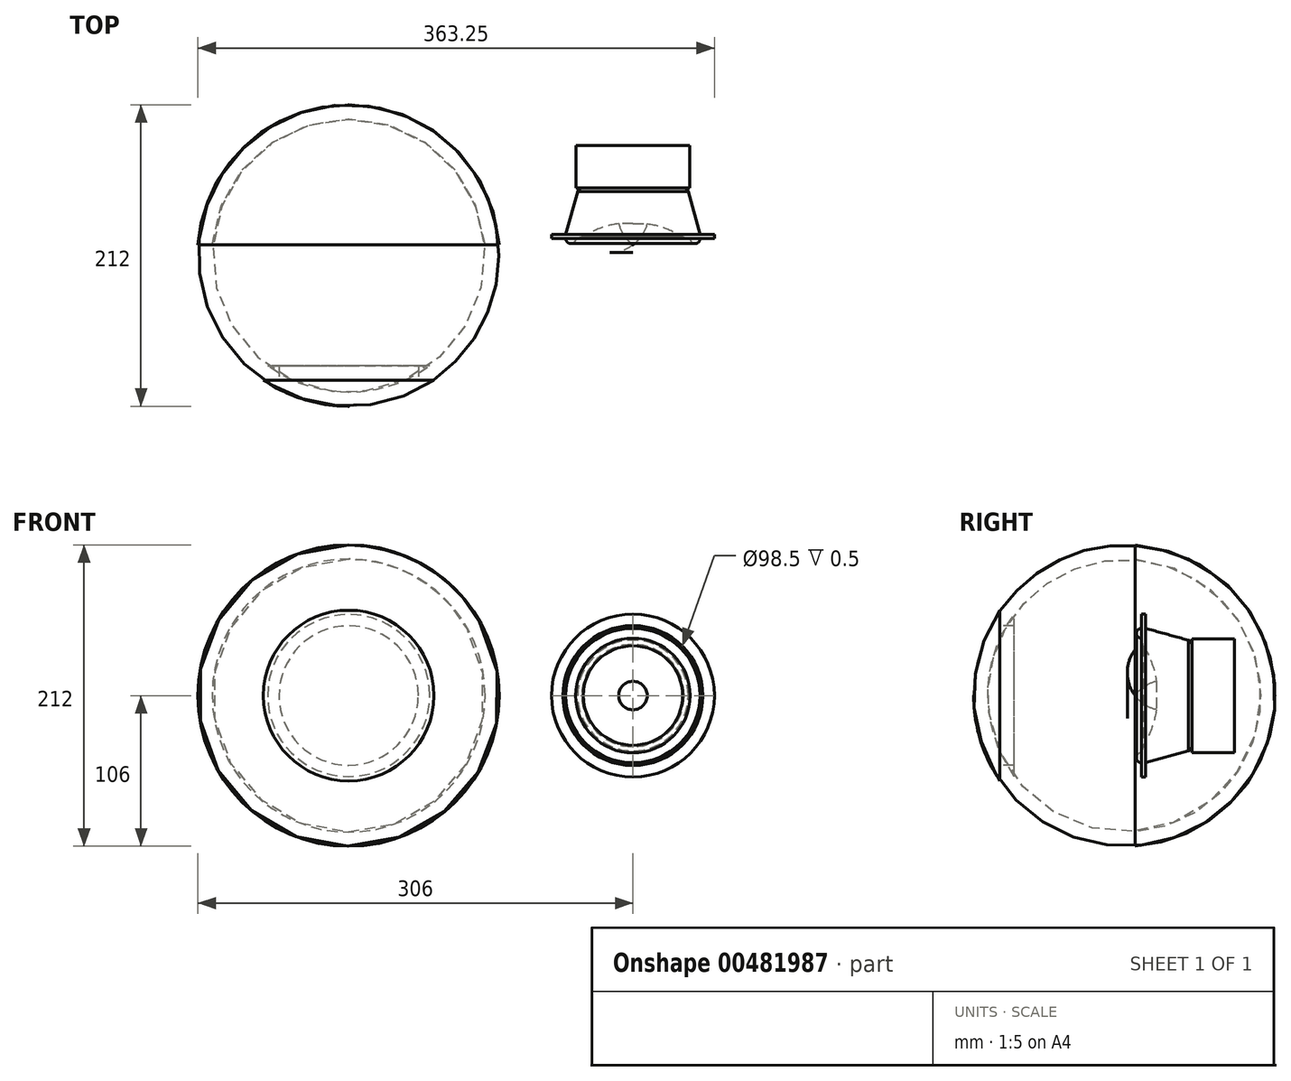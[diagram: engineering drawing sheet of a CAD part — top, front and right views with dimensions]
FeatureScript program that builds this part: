
annotation { "Feature Type Name" : "Feature", "Feature Type Description" : "" }
export const myFeature = defineFeature(function(context is Context, id is Id, definition is map)
    precondition{}
    {
        {
            var Q0;
            Q0=qCreatedBy(makeId("Top.planeOp"),FACE);
            var sketch = newSketch(context, id + "F0", { "sketchPlane" : qUnion([Q0])});
            skLineSegment(sketch, "E0", {"start": v(0, -95) * mm, "end": v(60, -95) * mm});
            skArc(sketch, "E1", {"start": v(60, -95) * mm, "mid": v(95.67, -53.63) * mm, "end": v(106, 0) * mm});
            skLineSegment(sketch, "E2", {"start": v(0, -95) * mm, "end": v(0, -85) * mm});
            skLineSegment(sketch, "E3", {"start": v(0, -85) * mm, "end": v(57, -85) * mm});
            skArc(sketch, "E4", {"start": v(57, -85) * mm, "mid": v(87.55, -47.57) * mm, "end": v(96, 0) * mm});
            skLineSegment(sketch, "E5", {"start": v(96, 0) * mm, "end": v(106, 0) * mm});
            skSolve(sketch);
        }
        {
            var Q0;
            Q0=qCreatedBy(makeId("Top.planeOp"),FACE);
            var sketch = newSketch(context, id + "F1", { "sketchPlane" : qUnion([Q0])});
            skLineSegment(sketch, "E6", {"start": v(0, -13) * mm, "end": v(0, 107) * mm, "construction": true});
            skSolve(sketch);
        }
        {
            var Q0;
            Q0 = qSketchRegion(id + "F0", true);
            var Q1;
            Q1=sQuery(id+"F1.wireOp",EDGE,"E6");
            var Q2;
            Q2=sQuery(id+"F1.wireOp",EDGE,"E6");
            revolve(context, id + "F2", {"entities" : qUnion([Q0]), "surfaceEntities" : qUnion([Q1]), "axis" : qUnion([Q2]), "revolveType" : RevolveType.FULL});
        }
        {
            var Q0;
            Q0=qCreatedBy(makeId("Top.planeOp"),FACE);
            var sketch = newSketch(context, id + "F3", { "sketchPlane" : qUnion([Q0])});
            skLineSegment(sketch, "E7", {"start": v(200, 70) * mm, "end": v(240, 70) * mm});
            skLineSegment(sketch, "E8", {"start": v(240, 70) * mm, "end": v(240, 40) * mm});
            skLineSegment(sketch, "E9", {"start": v(240, 40) * mm, "end": v(236, 40) * mm});
            skArc(sketch, "E10", {"start": v(200, 0) * mm, "mid": v(206.29, 6.64) * mm, "end": v(210, 15) * mm});
            skArc(sketch, "E11", {"start": v(235, 5.72) * mm, "mid": v(223.02, 11.76) * mm, "end": v(210, 15) * mm});
            skArc(sketch, "E12", {"start": v(240.25, 4.5) * mm, "mid": v(243.75, 1) * mm, "end": v(247.25, 4.5) * mm});
            skLineSegment(sketch, "E13", {"start": v(235, 5.72) * mm, "end": v(240.25, 4.5) * mm});
            skLineSegment(sketch, "E14", {"start": v(247.25, 4.5) * mm, "end": v(248.75, 4.5) * mm});
            skLineSegment(sketch, "E15", {"start": v(248.75, 4.5) * mm, "end": v(248.75, 5) * mm});
            skLineSegment(sketch, "E16", {"start": v(248.75, 5) * mm, "end": v(249.25, 5) * mm});
            skLineSegment(sketch, "E17", {"start": v(249.25, 5) * mm, "end": v(249.25, 4.5) * mm});
            skLineSegment(sketch, "E18", {"start": v(249.25, 4.5) * mm, "end": v(257.25, 4.5) * mm});
            skPoint(sketch, "E18.endSnap0", {"position": v(248, 4.5) * mm});
            skLineSegment(sketch, "E19", {"start": v(257.25, 7.5) * mm, "end": v(247.25, 7.5) * mm});
            skLineSegment(sketch, "E20", {"start": v(257.25, 4.5) * mm, "end": v(257.25, 7.5) * mm});
            skArc(sketch, "E21", {"start": v(238.92, 37.7) * mm, "mid": v(237.86, 39.35) * mm, "end": v(236, 40) * mm});
            skLineSegment(sketch, "E22", {"start": v(238.92, 37.7) * mm, "end": v(247.25, 7.5) * mm});
            skLineSegment(sketch, "E23", {"start": v(200, 70) * mm, "end": v(200, 0) * mm});
            skSolve(sketch);
        }
        {
            var Q0;
            Q0=qCreatedBy(makeId("Top.planeOp"),FACE);
            var sketch = newSketch(context, id + "F4", { "sketchPlane" : qUnion([Q0])});
            skLineSegment(sketch, "E24", {"start": v(200, 92.17) * mm, "end": v(200, -27.83) * mm, "construction": true});
            skSolve(sketch);
        }
        {
            var Q0;
            Q0 = qSketchRegion(id + "F3", true);
            var Q1;
            Q1=sQuery(id+"F4.wireOp",EDGE,"E24");
            revolve(context, id + "F5", {"entities" : qUnion([Q0]), "axis" : qUnion([Q1]), "revolveType" : RevolveType.FULL});
        }
        {
            var Q0;
            Q0=makeQuery(id+"F2.opRevolve","SWEPT_FACE",FACE,{"disambiguationData":[OSD([sQuery(id+"F0.wireOp",EDGE,"E0")])]});
            var sketch = newSketch(context, id + "F6", { "sketchPlane" : qUnion([Q0])});
            skCircle(sketch, "E25", {"center": v(0, 0) * mm, "radius": 49 * mm});
            skSolve(sketch);
        }
        {
            var Q0;
            Q0 = qSketchRegion(id + "F6", true);
            extrude(context, id + "F7", {"entities" : qUnion([Q0]), "operationType" : NewBodyOperationType.REMOVE, "oppositeDirection" : true, "depth" : 10 * mm});
        }
    });
